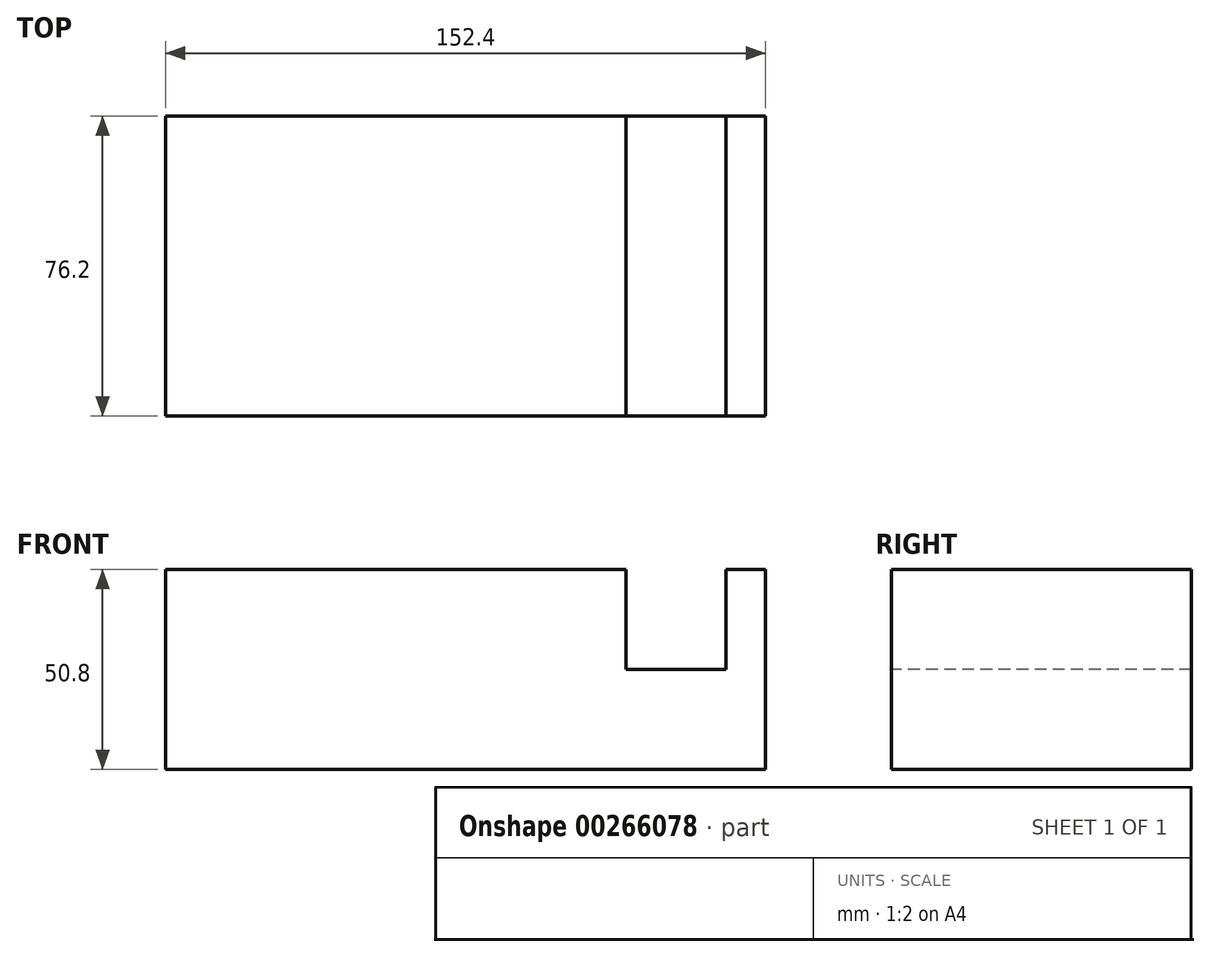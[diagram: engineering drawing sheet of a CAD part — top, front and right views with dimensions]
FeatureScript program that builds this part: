
annotation { "Feature Type Name" : "Feature", "Feature Type Description" : "" }
export const myFeature = defineFeature(function(context is Context, id is Id, definition is map)
    precondition{}
    {
        {
            var Q0;
            Q0=qCreatedBy(makeId("Front.planeOp"),FACE);
            var sketch = newSketch(context, id + "F0", { "sketchPlane" : qUnion([Q0])});
            skLineSegment(sketch, "E0.bottom", {"start": v(-79.87, 53.68) * mm, "end": v(72.53, 53.68) * mm});
            skLineSegment(sketch, "E0.top", {"start": v(-79.87, 2.88) * mm, "end": v(72.53, 2.88) * mm});
            skLineSegment(sketch, "E0.left", {"start": v(-79.87, 53.68) * mm, "end": v(-79.87, 2.88) * mm});
            skLineSegment(sketch, "E0.right", {"start": v(72.53, 53.68) * mm, "end": v(72.53, 2.88) * mm});
            skSolve(sketch);
        }
        {
            var Q0;
            Q0=makeQuery(id+"F0.imprint","IMPRINT",FACE,{"disambiguationData":[TD([[makeQuery(id+"F0.imprint","IMPRINT",EDGE,{"derivedFrom":sQuery(id+"F0.wireOp",EDGE,"E0.bottom")}),-1.0]])]});
            extrude(context, id + "F1", {"entities" : qUnion([Q0]), "depth" : 76.2 * mm});
        }
        {
            var Q0;
            Q0=makeQuery(id+"F1.opExtrude","CAP_FACE",FACE,{"disambiguationData":[OSD([sQuery(id+"F0.wireOp",EDGE,"E0.bottom"),sQuery(id+"F0.wireOp",EDGE,"E0.top"),sQuery(id+"F0.wireOp",EDGE,"E0.left"),sQuery(id+"F0.wireOp",EDGE,"E0.right")])],"isStart":false});
            var sketch = newSketch(context, id + "F2", { "sketchPlane" : qUnion([Q0])});
            skLineSegment(sketch, "E1.bottom", {"start": v(62.5, 53.68) * mm, "end": v(37.1, 53.68) * mm});
            skLineSegment(sketch, "E1.top", {"start": v(62.5, 28.28) * mm, "end": v(37.1, 28.28) * mm});
            skLineSegment(sketch, "E1.left", {"start": v(62.5, 53.68) * mm, "end": v(62.5, 28.28) * mm});
            skLineSegment(sketch, "E1.right", {"start": v(37.1, 53.68) * mm, "end": v(37.1, 28.28) * mm});
            skSolve(sketch);
        }
        {
            var Q0;
            Q0=makeQuery(id+"F2.imprint","IMPRINT",FACE,{"disambiguationData":[TD([[makeQuery(id+"F2.imprint","IMPRINT",EDGE,{"derivedFrom":sQuery(id+"F2.wireOp",EDGE,"E1.bottom")}),-1.0]])]});
            extrude(context, id + "F3", {"entities" : qUnion([Q0]), "operationType" : NewBodyOperationType.REMOVE, "endBound" : BoundingType.UP_TO_NEXT, "oppositeDirection" : true, "depth" : 25.4 * mm});
        }
    });
